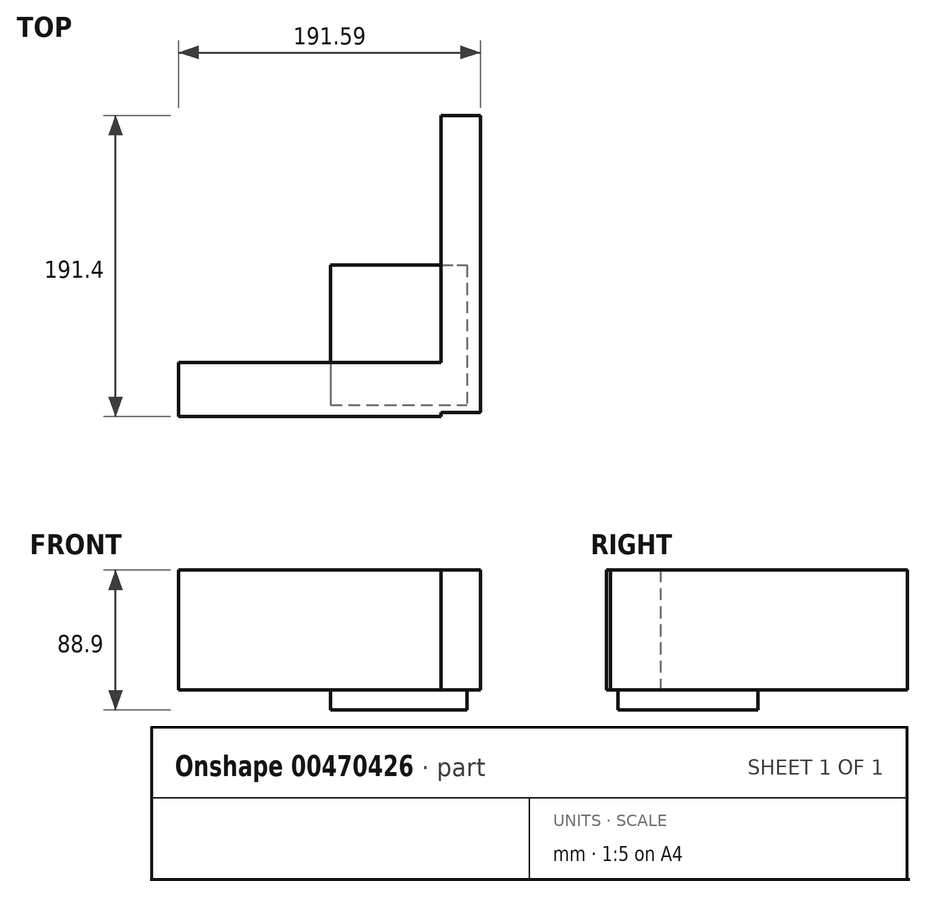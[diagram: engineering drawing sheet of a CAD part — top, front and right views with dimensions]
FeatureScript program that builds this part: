
annotation { "Feature Type Name" : "Feature", "Feature Type Description" : "" }
export const myFeature = defineFeature(function(context is Context, id is Id, definition is map)
    precondition{}
    {
        {
            var Q0;
            Q0=qCreatedBy(makeId("Top.planeOp"),FACE);
            var sketch = newSketch(context, id + "F0", { "sketchPlane" : qUnion([Q0])});
            skLineSegment(sketch, "E0.bottom", {"start": v(95.26, 95.1) * mm, "end": v(70.4, 95.1) * mm});
            skLineSegment(sketch, "E0.top", {"start": v(95.26, -93.75) * mm, "end": v(70.4, -93.75) * mm});
            skLineSegment(sketch, "E0.left", {"start": v(95.26, 95.1) * mm, "end": v(95.26, -93.75) * mm});
            skLineSegment(sketch, "E0.right", {"start": v(70.4, 95.1) * mm, "end": v(70.4, -93.75) * mm});
            skLineSegment(sketch, "E1.bottom", {"start": v(-96.33, -96.3) * mm, "end": v(70.4, -96.3) * mm});
            skLineSegment(sketch, "E1.top", {"start": v(-96.33, -62.02) * mm, "end": v(70.4, -62.02) * mm});
            skLineSegment(sketch, "E1.left", {"start": v(-96.33, -96.3) * mm, "end": v(-96.33, -62.02) * mm});
            skLineSegment(sketch, "E1.right", {"start": v(70.4, -96.3) * mm, "end": v(70.4, -62.02) * mm});
            skSolve(sketch);
        }
        {
            var Q0;
            Q0=makeQuery(id+"F0.imprint","IMPRINT",FACE,{"disambiguationData":[TD([[makeQuery(id+"F0.imprint","IMPRINT",EDGE,{"derivedFrom":sQuery(id+"F0.wireOp",EDGE,"E0.bottom")}),1.0]])]});
            var Q1;
            Q1 = qSketchRegion(id + "F0", true);
            extrude(context, id + "F1", {"entities" : qUnion([Q0, Q1]), "depth" : 76.2 * mm});
        }
        {
            var Q0;
            Q0=qCreatedBy(makeId("Top.planeOp"),FACE);
            var sketch = newSketch(context, id + "F2", { "sketchPlane" : qUnion([Q0])});
            skLineSegment(sketch, "E2.bottom", {"start": v(0, 0) * mm, "end": v(86.73, 0) * mm});
            skLineSegment(sketch, "E2.top", {"start": v(0, -88.8) * mm, "end": v(86.73, -88.8) * mm});
            skLineSegment(sketch, "E2.left", {"start": v(0, 0) * mm, "end": v(0, -88.8) * mm});
            skLineSegment(sketch, "E2.right", {"start": v(86.73, 0) * mm, "end": v(86.73, -88.8) * mm});
            skSolve(sketch);
        }
        {
            var Q0;
            Q0 = qSketchRegion(id + "F2", true);
            extrude(context, id + "F3", {"entities" : qUnion([Q0]), "operationType" : NewBodyOperationType.ADD, "oppositeDirection" : true, "depth" : 12.7 * mm});
        }
    });
